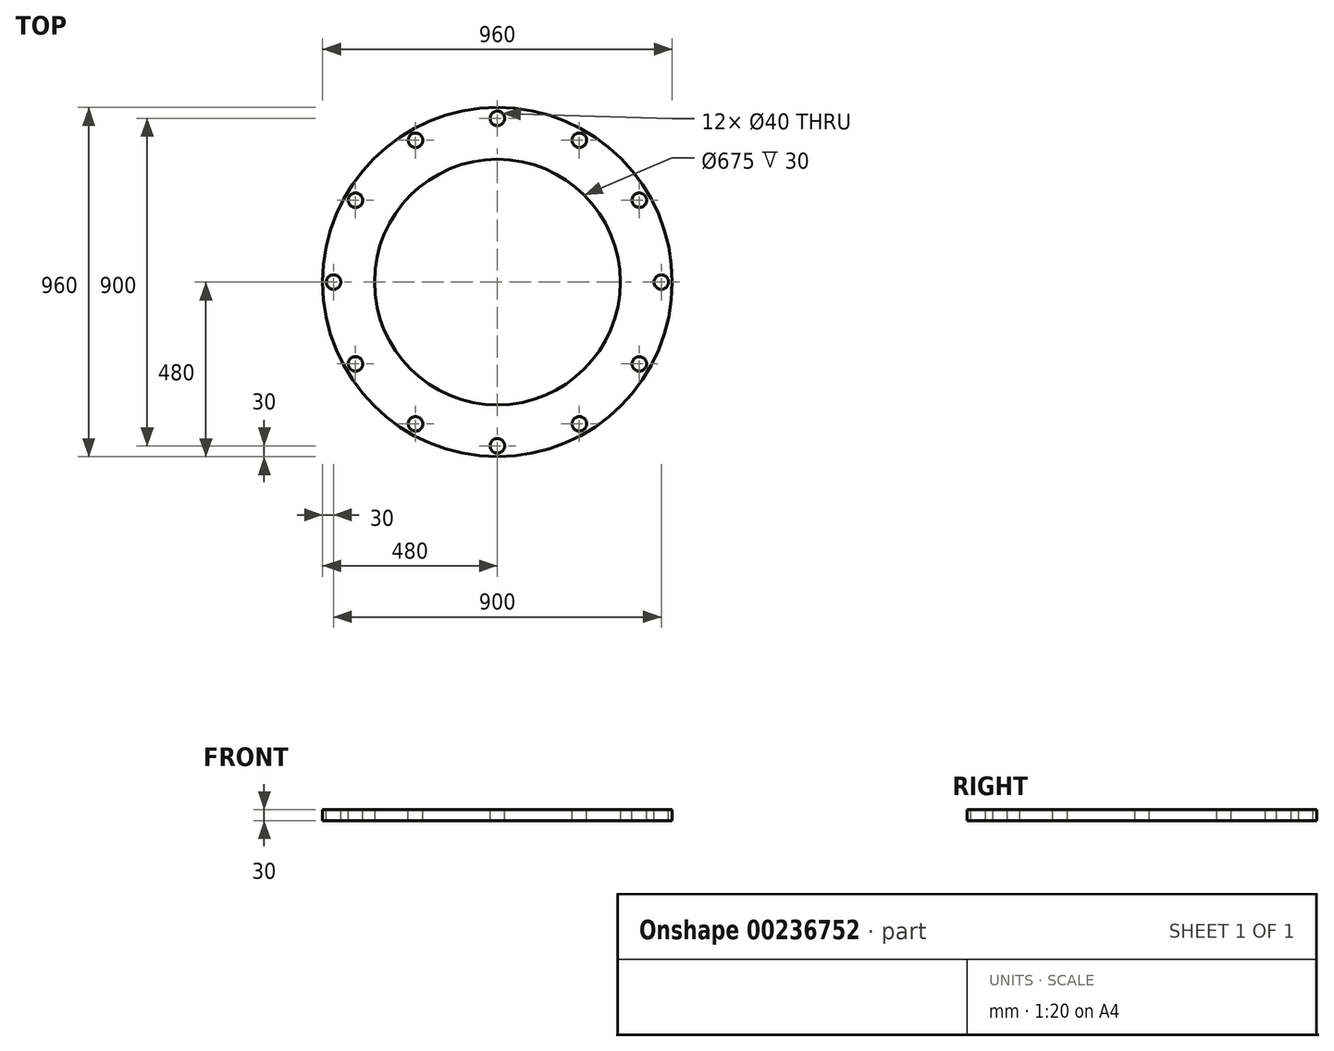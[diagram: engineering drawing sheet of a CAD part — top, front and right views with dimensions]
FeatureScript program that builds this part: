
annotation { "Feature Type Name" : "Feature", "Feature Type Description" : "" }
export const myFeature = defineFeature(function(context is Context, id is Id, definition is map)
    precondition{}
    {
        {
            var Q0;
            Q0=qCreatedBy(makeId("Top.planeOp"),FACE);
            var sketch = newSketch(context, id + "F0", { "sketchPlane" : qUnion([Q0])});
            skCircle(sketch, "E0", {"center": v(0, 0) * mm, "radius": 480 * mm});
            skCircle(sketch, "E1", {"center": v(0, 0) * mm, "radius": 337.5 * mm});
            skSolve(sketch);
        }
        {
            var Q0;
            Q0 = qSketchRegion(id + "F0", true);
            extrude(context, id + "F1", {"entities" : qUnion([Q0]), "depth" : 30 * mm, "offsetDistance" : 25 * mm});
        }
        {
            var Q0;
            Q0=makeQuery(id+"F1.opExtrude","CAP_FACE",FACE,{"disambiguationData":[OSD([sQuery(id+"F0.wireOp",EDGE,"E0"),sQuery(id+"F0.wireOp",EDGE,"E1")])],"isStart":false});
            var sketch = newSketch(context, id + "F2", { "sketchPlane" : qUnion([Q0])});
            skCircle(sketch, "E2", {"center": v(0, 0) * mm, "radius": 450 * mm, "construction": true});
            skLineSegment(sketch, "E3", {"start": v(0, 508.54) * mm, "end": v(0, -521.55) * mm, "construction": true});
            skLineSegment(sketch, "E4", {"start": v(517.95, 0) * mm, "end": v(-584.94, 0) * mm, "construction": true});
            skCircle(sketch, "E5", {"center": v(-450, 0) * mm, "radius": 20 * mm});
            skCircle(sketch, "E6.1.0", {"center": v(-389.71, -225) * mm, "radius": 20 * mm});
            skCircle(sketch, "E6.2.0", {"center": v(-225, -389.71) * mm, "radius": 20 * mm});
            skCircle(sketch, "E6.3.0", {"center": v(0, -450) * mm, "radius": 20 * mm});
            skCircle(sketch, "E6.4.0", {"center": v(225, -389.71) * mm, "radius": 20 * mm});
            skCircle(sketch, "E6.5.0", {"center": v(389.71, -225) * mm, "radius": 20 * mm});
            skCircle(sketch, "E6.6.0", {"center": v(450, 0) * mm, "radius": 20 * mm});
            skCircle(sketch, "E6.7.0", {"center": v(389.71, 225) * mm, "radius": 20 * mm});
            skCircle(sketch, "E6.8.0", {"center": v(225, 389.71) * mm, "radius": 20 * mm});
            skCircle(sketch, "E6.9.0", {"center": v(0, 450) * mm, "radius": 20 * mm});
            skCircle(sketch, "E6.10.0", {"center": v(-225, 389.71) * mm, "radius": 20 * mm});
            skCircle(sketch, "E6.11.0", {"center": v(-389.71, 225) * mm, "radius": 20 * mm});
            skSolve(sketch);
        }
        {
            var Q0;
            Q0=makeQuery(id+"F2.imprint","IMPRINT",FACE,{"disambiguationData":[TD([[makeQuery(id+"F2.imprint","IMPRINT",EDGE,{"derivedFrom":sQuery(id+"F2.wireOp",EDGE,"E6.11.0")}),1.0]])]});
            var Q1;
            Q1=makeQuery(id+"F2.imprint","IMPRINT",FACE,{"disambiguationData":[TD([[makeQuery(id+"F2.imprint","IMPRINT",EDGE,{"derivedFrom":sQuery(id+"F2.wireOp",EDGE,"E5")}),1.0]])]});
            var Q2;
            Q2=makeQuery(id+"F2.imprint","IMPRINT",FACE,{"disambiguationData":[TD([[makeQuery(id+"F2.imprint","IMPRINT",EDGE,{"derivedFrom":sQuery(id+"F2.wireOp",EDGE,"E6.1.0")}),1.0]])]});
            var Q3;
            Q3=makeQuery(id+"F2.imprint","IMPRINT",FACE,{"disambiguationData":[TD([[makeQuery(id+"F2.imprint","IMPRINT",EDGE,{"derivedFrom":sQuery(id+"F2.wireOp",EDGE,"E6.2.0")}),1.0]])]});
            var Q4;
            Q4=makeQuery(id+"F2.imprint","IMPRINT",FACE,{"disambiguationData":[TD([[makeQuery(id+"F2.imprint","IMPRINT",EDGE,{"derivedFrom":sQuery(id+"F2.wireOp",EDGE,"E6.3.0")}),1.0]])]});
            var Q5;
            Q5=makeQuery(id+"F2.imprint","IMPRINT",FACE,{"disambiguationData":[TD([[makeQuery(id+"F2.imprint","IMPRINT",EDGE,{"derivedFrom":sQuery(id+"F2.wireOp",EDGE,"E6.4.0")}),1.0]])]});
            var Q6;
            Q6=makeQuery(id+"F2.imprint","IMPRINT",FACE,{"disambiguationData":[TD([[makeQuery(id+"F2.imprint","IMPRINT",EDGE,{"derivedFrom":sQuery(id+"F2.wireOp",EDGE,"E6.5.0")}),1.0]])]});
            var Q7;
            Q7=makeQuery(id+"F2.imprint","IMPRINT",FACE,{"disambiguationData":[TD([[makeQuery(id+"F2.imprint","IMPRINT",EDGE,{"derivedFrom":sQuery(id+"F2.wireOp",EDGE,"E6.6.0")}),1.0]])]});
            var Q8;
            Q8=makeQuery(id+"F2.imprint","IMPRINT",FACE,{"disambiguationData":[TD([[makeQuery(id+"F2.imprint","IMPRINT",EDGE,{"derivedFrom":sQuery(id+"F2.wireOp",EDGE,"E6.7.0")}),1.0]])]});
            var Q9;
            Q9=makeQuery(id+"F2.imprint","IMPRINT",FACE,{"disambiguationData":[TD([[makeQuery(id+"F2.imprint","IMPRINT",EDGE,{"derivedFrom":sQuery(id+"F2.wireOp",EDGE,"E6.8.0")}),1.0]])]});
            var Q10;
            Q10=makeQuery(id+"F2.imprint","IMPRINT",FACE,{"disambiguationData":[TD([[makeQuery(id+"F2.imprint","IMPRINT",EDGE,{"derivedFrom":sQuery(id+"F2.wireOp",EDGE,"E6.9.0")}),1.0]])]});
            var Q11;
            Q11=makeQuery(id+"F2.imprint","IMPRINT",FACE,{"disambiguationData":[TD([[makeQuery(id+"F2.imprint","IMPRINT",EDGE,{"derivedFrom":sQuery(id+"F2.wireOp",EDGE,"E6.10.0")}),1.0]])]});
            extrude(context, id + "F3", {"entities" : qUnion([Q0, Q1, Q2, Q3, Q4, Q5, Q6, Q7, Q8, Q9, Q10, Q11]), "operationType" : NewBodyOperationType.REMOVE, "endBound" : BoundingType.THROUGH_ALL, "oppositeDirection" : true, "depth" : 25 * mm, "offsetDistance" : 25 * mm});
        }
    });
